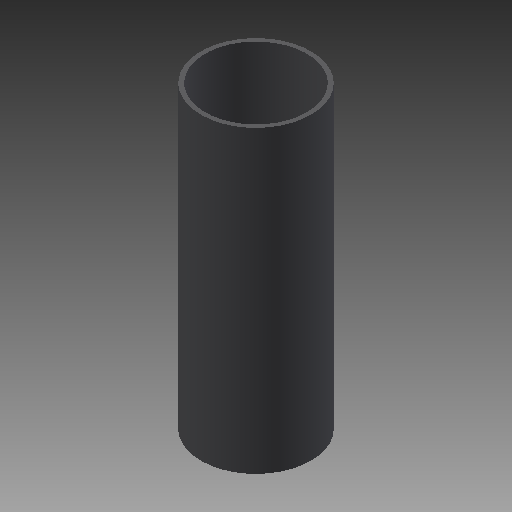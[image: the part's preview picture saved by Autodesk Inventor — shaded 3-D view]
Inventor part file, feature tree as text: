
AUTODESK INVENTOR PART (.ipt)
format: ipt  version: 2017 (Build 210142000, 142)  size: 95,744 bytes
history: native  units: in
note: dims shown in document units (in); Inventor stores cm internally (conversion verified against a paired STEP export)
features: other x14, revolve x1, sketch x1
ambient origin geometry x8: Origin, YZ Plane, XZ Plane, XY Plane, X Axis, Y Axis, Z Axis, Center Point
bodies: Solid1 (feature_tree)
feature tree (16):
  revolve  "Revolution1"  [1 undecoded]
  other  "tube_rear_XY"
  other  "tube_rear_YZ"
  other  "tube_rear_ZX"
  other  "tube_rear_X"
  other  "tube_rear_Y"
  other  "tube_rear_Z"
  other  "tube_rear_Center"
  other  "tube_rod_guide_XY"
  other  "tube_rod_guide_YZ"
  other  "tube_rod_guide_ZX"
  other  "tube_rod_guide_X"
  other  "tube_rod_guide_Y"
  other  "tube_rod_guide_Z"
  other  "tube_rod_guide_Center"
  sketch  "Sketch_4"  dims[d0=360.0deg d1=0.0in d2=0.0in]
note: 1 required parameter value undecoded (feature->parameter linkage not recoverable at this tier; creation-order binding heuristic only, values carry confidence <= 0.55)
